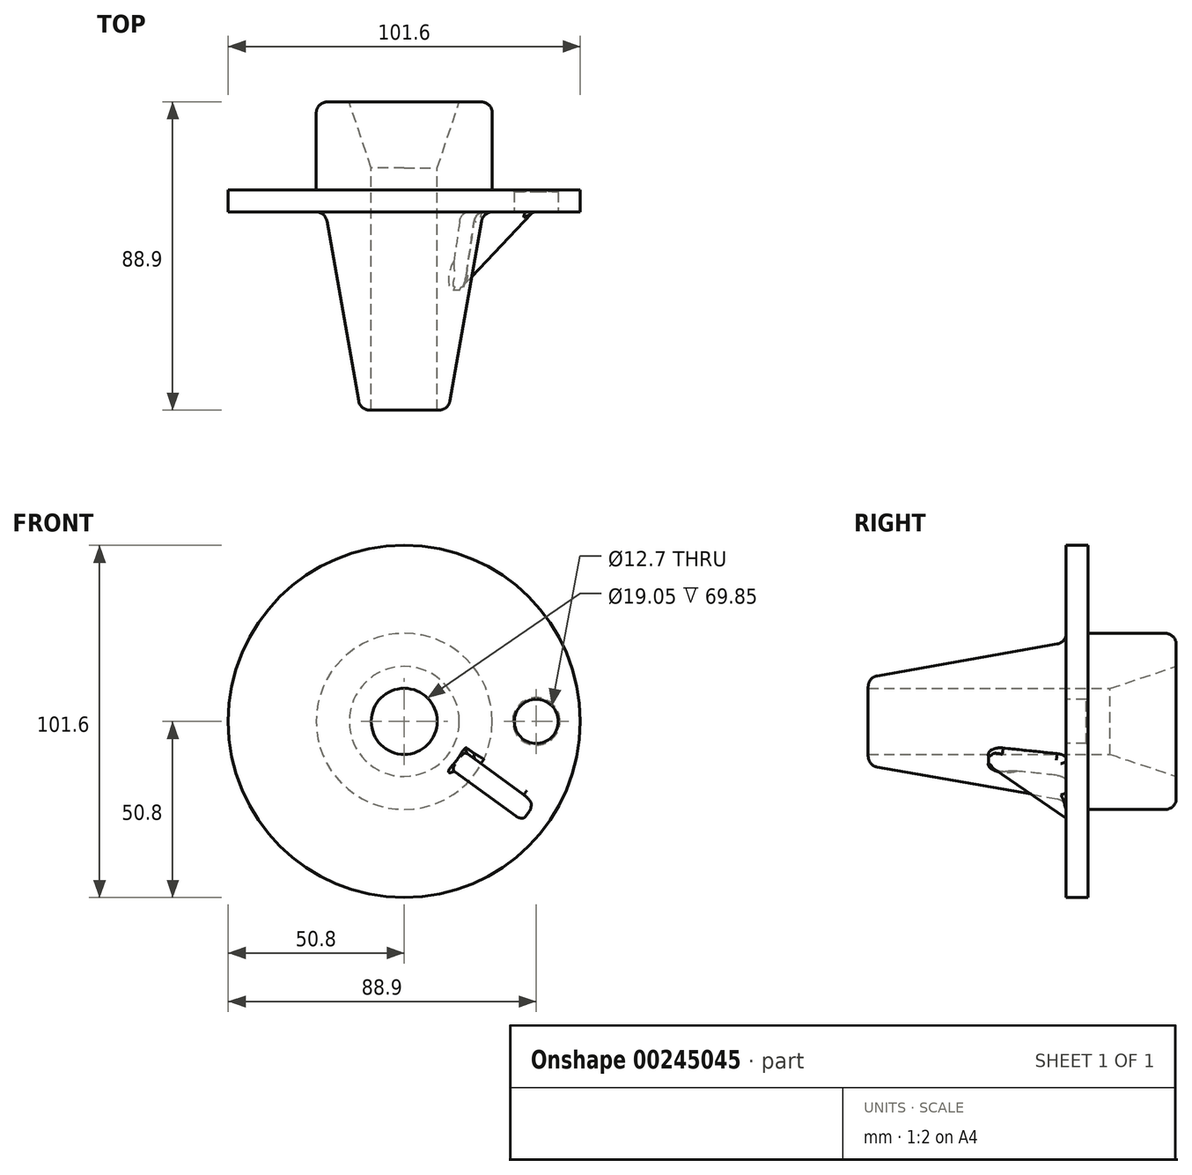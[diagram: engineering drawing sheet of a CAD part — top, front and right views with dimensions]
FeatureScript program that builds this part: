
annotation { "Feature Type Name" : "Feature", "Feature Type Description" : "" }
export const myFeature = defineFeature(function(context is Context, id is Id, definition is map)
    precondition{}
    {
        {
            var Q0;
            Q0=qCreatedBy(makeId("Right.planeOp"),FACE);
            var sketch = newSketch(context, id + "F0", { "sketchPlane" : qUnion([Q0])});
            skLineSegment(sketch, "E0", {"start": v(0, 50.8) * mm, "end": v(0, 25.44) * mm});
            skLineSegment(sketch, "E1", {"start": v(-2.62, 22.31) * mm, "end": v(-57.15, 12.7) * mm});
            skLineSegment(sketch, "E2", {"start": v(-57.15, 12.7) * mm, "end": v(-57.15, 0) * mm});
            skLineSegment(sketch, "E3", {"start": v(12.7, 0) * mm, "end": v(12.7, 9.53) * mm});
            skLineSegment(sketch, "E4", {"start": v(12.7, 9.53) * mm, "end": v(31.75, 15.88) * mm});
            skLineSegment(sketch, "E5", {"start": v(31.75, 15.88) * mm, "end": v(31.75, 25.4) * mm});
            skLineSegment(sketch, "E6", {"start": v(31.75, 25.4) * mm, "end": v(6.35, 25.4) * mm});
            skLineSegment(sketch, "E7", {"start": v(6.35, 25.4) * mm, "end": v(6.35, 50.8) * mm});
            skLineSegment(sketch, "E8", {"start": v(6.35, 50.8) * mm, "end": v(0, 50.8) * mm});
            skLineSegment(sketch, "E9", {"start": v(-57.15, 0) * mm, "end": v(31.75, 0) * mm, "construction": true});
            skLineSegment(sketch, "E10", {"start": v(-57.15, 0) * mm, "end": v(12.7, 0) * mm});
            skPoint(sketch, "E11.visualSharp", {"position": v(0, 22.78) * mm});
            skArc(sketch, "E11.filletArc", {"start": v(-2.62, 22.31) * mm, "mid": v(-0.74, 23.4) * mm, "end": v(0, 25.44) * mm});
            skSolve(sketch);
        }
        {
            var Q0;
            Q0=makeQuery(id+"F0.imprint","IMPRINT",FACE,{"disambiguationData":[TD([[makeQuery(id+"F0.imprint","IMPRINT",EDGE,{"derivedFrom":sQuery(id+"F0.wireOp",EDGE,"E0")}),1.0]])]});
            var Q1;
            Q1=sQuery(id+"F0.wireOp",EDGE,"E9");
            revolve(context, id + "F1", {"entities" : qUnion([Q0]), "axis" : qUnion([Q1]), "revolveType" : RevolveType.FULL});
        }
        {
            var Q0;
            Q0=makeQuery(id+"F1.opRevolve","SWEPT_FACE",FACE,{"disambiguationData":[OSD([sQuery(id+"F0.wireOp",EDGE,"E0")])]});
            var sketch = newSketch(context, id + "F2", { "sketchPlane" : qUnion([Q0])});
            skCircle(sketch, "E12", {"center": v(38.1, 0) * mm, "radius": 6.35 * mm});
            skSolve(sketch);
        }
        {
            var Q0;
            Q0=qSketchRegion(id+"F2",true);
            extrude(context, id + "F3", {"entities" : qUnion([Q0]), "operationType" : NewBodyOperationType.REMOVE, "endBound" : BoundingType.THROUGH_ALL, "oppositeDirection" : true, "depth" : 25.4 * mm});
        }
        {
            var Q0;
            Q0=makeQuery(id+"F3.boolean.opBoolean","COPY",EDGE,{"derivedFrom":makeQuery(id+"F3.opExtrude","CAP_EDGE",EDGE,{"disambiguationData":[OSD([sQuery(id+"F2.wireOp",EDGE,"E12")])],"isStart":true})});
            var Q1;
            Q1=makeQuery(id+"F3.boolean.opBoolean","INTERSECT",EDGE,{"derivedFrom":[makeQuery(id+"F1.opRevolve","SWEPT_FACE",FACE,{"disambiguationData":[OSD([sQuery(id+"F0.wireOp",EDGE,"E7")])]}),makeQuery(id+"F3.opExtrude","SWEPT_FACE",FACE,{"disambiguationData":[OSD([sQuery(id+"F2.wireOp",EDGE,"E12")])]})]});
            chamfer(context, id + "F4", {"entities" : qUnion([Q0, Q1]), "width" : 0.5 * mm, "tangentPropagation" : true});
        }
        {
            var Q0;
            Q0=qCreatedBy(makeId("Top.planeOp"),FACE);
            var Q1;
            Q1=sQuery(id+"F0.wireOp",EDGE,"E9");
            cPlane(context, id + "F5", {"entities" : qUnion([Q0, Q1]), "cplaneType" : CPlaneType.LINE_ANGLE, "offset" : 25.4 * mm, "angle" : 36 * degree, "width" : 152.4 * mm, "height" : 152.4 * mm});
        }
        {
            var Q0;
            Q0=qCreatedBy(id+"F5.planeOp",FACE);
            var sketch = newSketch(context, id + "F6", { "sketchPlane" : qUnion([Q0])});
            skLineSegment(sketch, "E13", {"start": v(44.45, 0) * mm, "end": v(0, 0) * mm});
            skLineSegment(sketch, "E14", {"start": v(0, 0) * mm, "end": v(0, 38.1) * mm});
            skLineSegment(sketch, "E15", {"start": v(0, 38.1) * mm, "end": v(44.45, 0) * mm});
            skSolve(sketch);
        }
        {
            var Q0;
            Q0=makeQuery(id+"F6.imprint","IMPRINT",FACE,{"disambiguationData":[TD([[makeQuery(id+"F6.imprint","IMPRINT",EDGE,{"derivedFrom":sQuery(id+"F6.wireOp",EDGE,"E13")}),-1.0]])]});
            extrude(context, id + "F7", {"entities" : qUnion([Q0]), "operationType" : NewBodyOperationType.ADD, "depth" : 6.35 * mm, "symmetric" : true});
        }
        {
            var Q0;
            Q0=makeQuery(id+"F7.opExtrude","CAP_EDGE",EDGE,{"disambiguationData":[OSD([sQuery(id+"F6.wireOp",EDGE,"E13")])],"isStart":false});
            var Q1;
            Q1=makeQuery(id+"F7.boolean.opBoolean","INTERSECT",EDGE,{"derivedFrom":[makeQuery(id+"F1.opRevolve","SWEPT_FACE",FACE,{"disambiguationData":[OSD([sQuery(id+"F0.wireOp",EDGE,"E1")])]}),makeQuery(id+"F7.opExtrude","SWEPT_FACE",FACE,{"disambiguationData":[OSD([sQuery(id+"F6.wireOp",EDGE,"E15")])]})]});
            var Q2;
            Q2=makeQuery(id+"F7.boolean.opBoolean","INTERSECT",EDGE,{"derivedFrom":[makeQuery(id+"F1.opRevolve","SWEPT_FACE",FACE,{"disambiguationData":[OSD([sQuery(id+"F0.wireOp",EDGE,"E1")])]}),makeQuery(id+"F7.opExtrude","CAP_FACE",FACE,{"disambiguationData":[OSD([sQuery(id+"F6.wireOp",EDGE,"E13"),sQuery(id+"F6.wireOp",EDGE,"E14"),sQuery(id+"F6.wireOp",EDGE,"E15")])],"isStart":true})]});
            var Q3;
            Q3=makeQuery(id+"F7.opExtrude","CAP_EDGE",EDGE,{"disambiguationData":[OSD([sQuery(id+"F6.wireOp",EDGE,"E15")])],"isStart":true});
            var Q4;
            Q4=makeQuery(id+"F7.opExtrude","CAP_EDGE",EDGE,{"disambiguationData":[OSD([sQuery(id+"F6.wireOp",EDGE,"E15")])],"isStart":false});
            fillet(context, id + "F8", {"entities" : qUnion([Q0, Q1, Q2, Q3, Q4]), "radius" : 1.52 * mm, "tangentPropagation" : true, "allowEdgeOverflow" : false});
        }
        {
            var Q0;
            Q0=makeQuery(id+"F1.opRevolve","SWEPT_FACE",FACE,{"disambiguationData":[OSD([sQuery(id+"F0.wireOp",EDGE,"E3")])]});
            extrude(context, id + "F9", {"entities" : qUnion([Q0]), "operationType" : NewBodyOperationType.REMOVE, "endBound" : BoundingType.THROUGH_ALL, "oppositeDirection" : true, "depth" : 25.4 * mm});
        }
        {
            var Q0;
            Q0=makeQuery(id+"F1.opRevolve","SWEPT_EDGE",EDGE,{"disambiguationData":[OSD([sQuery(id+"F0.wireOp",EDGE,"E1"),sQuery(id+"F0.wireOp",EDGE,"E2")])]});
            var Q1;
            Q1=makeQuery(id+"F1.opRevolve","SWEPT_EDGE",EDGE,{"disambiguationData":[OSD([sQuery(id+"F0.wireOp",EDGE,"E5"),sQuery(id+"F0.wireOp",EDGE,"E6")])]});
            fillet(context, id + "F10", {"entities" : qUnion([Q0, Q1]), "radius" : 3.17 * mm, "tangentPropagation" : true, "allowEdgeOverflow" : false});
        }
    });
